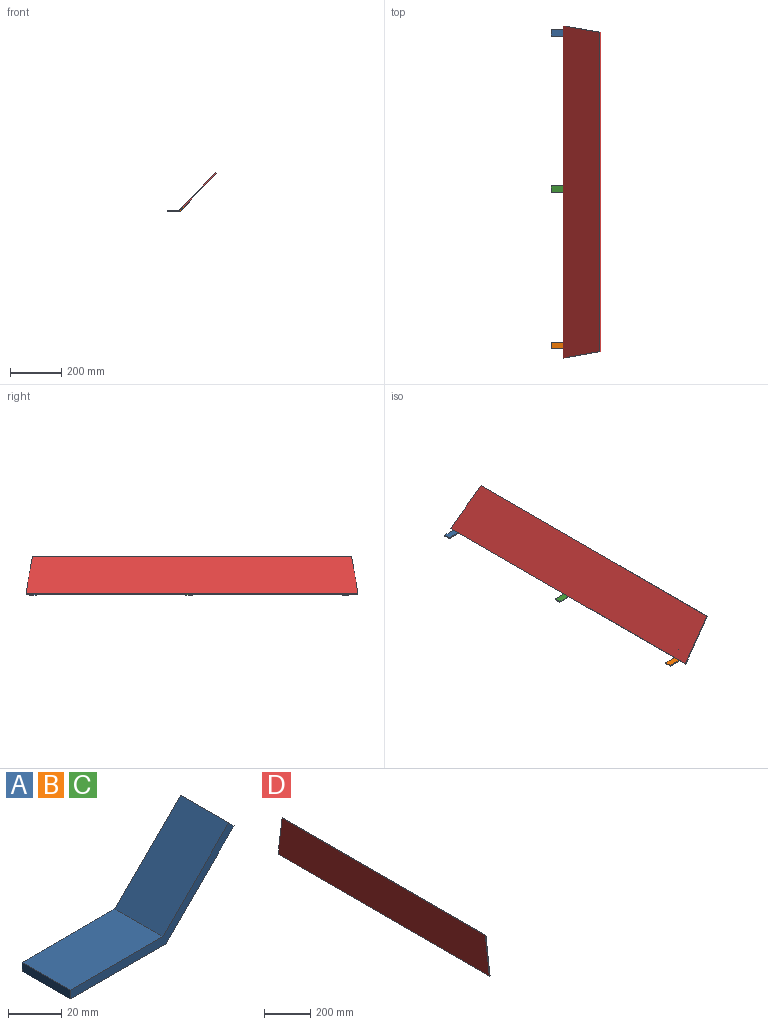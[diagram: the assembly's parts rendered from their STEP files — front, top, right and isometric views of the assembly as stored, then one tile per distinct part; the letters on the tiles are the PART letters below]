
ASSEMBLY  parts=4 mates=3
PART A: 8 faces, bbox 86.7x25.4x38.7 mm
  f0: plane 35.92x35.92mm, normal (0.71,0,-0.71), area 1290.3mm2, adj f1,f5,f6,f7
  f1: plane 25.4x2.82mm, normal (0.71,0,0.71), area 101.3mm2, adj f0,f2,f6,f7
  f2: plane 34.75x34.75mm, normal (-0.71,0,0.71), area 1248.4mm2, adj f1,f3,f6,f7
  f3: plane 49.15x25.4mm, normal (0,0,1), area 1248.4mm2, adj f2,f4,f6,f7
  f4: plane 25.4x3.99mm, normal (-1,0,0), area 101.3mm2, adj f3,f5,f6,f7
  f5: plane 50.8x25.4mm, normal (0,0,-1), area 1290.3mm2, adj f0,f4,f6,f7
  f6: plane 86.72x38.74mm, normal (0,-1,0), area 398.6mm2, adj f0,f1,f2,f3,f4,f5
  f7: plane 86.72x38.74mm, normal (0,1,0), area 398.6mm2, adj f0,f1,f2,f3,f4,f5
PART B: same geometry as A
PART C: same geometry as A
PART D: 6 faces, bbox 3.9x1295.4x203.2 mm
  f0: plane 1245.5x3.86mm, normal (0,0,1), area 4808.6mm2, adj f1,f3,f4,f5
  f1: plane 203.2x24.95mm, normal (0,-0.99,0.12), area 790.4mm2, adj f0,f2,f4,f5
  f2: plane 1295.4x3.86mm, normal (0,0,-1), area 5001.3mm2, adj f1,f3,f4,f5
  f3: plane 203.2x24.95mm, normal (0,0.99,0.12), area 790.4mm2, adj f0,f2,f4,f5
  f4: plane 1295.4x203.2mm, normal (1,0,0), area 258155.5mm2, adj f0,f1,f2,f3
  f5: plane 1295.4x203.2mm, normal (-1,0,0), area 258155.5mm2, adj f0,f1,f2,f3
PLACE A rot(axis=(0,-1,0),0.1deg) t=(-61.04,575.67,155.24)mm
PLACE B rot(axis=(0,-1,0),0.1deg) t=(-61.04,-643.53,155.24)mm
PLACE C rot(axis=(0,-1,0),0.1deg) t=(-61.04,-33.93,155.24)mm
PLACE D rot(axis=(0,1,0),44.9deg) t=(-252.19,-44.19,195.15)mm
MATE parallel B.f0 <-> C.f0  axis (0.71,0,-0.71) through (-247.47,-643.53,188.76)mm
MATE parallel A.f0 <-> C.f0  axis (0.71,0,-0.71) through (-247.47,550.27,188.76)mm
MATE parallel C.f2 <-> D.f4  axis (-0.71,0,0.71) through (-267.06,-46.63,174.76)mm
